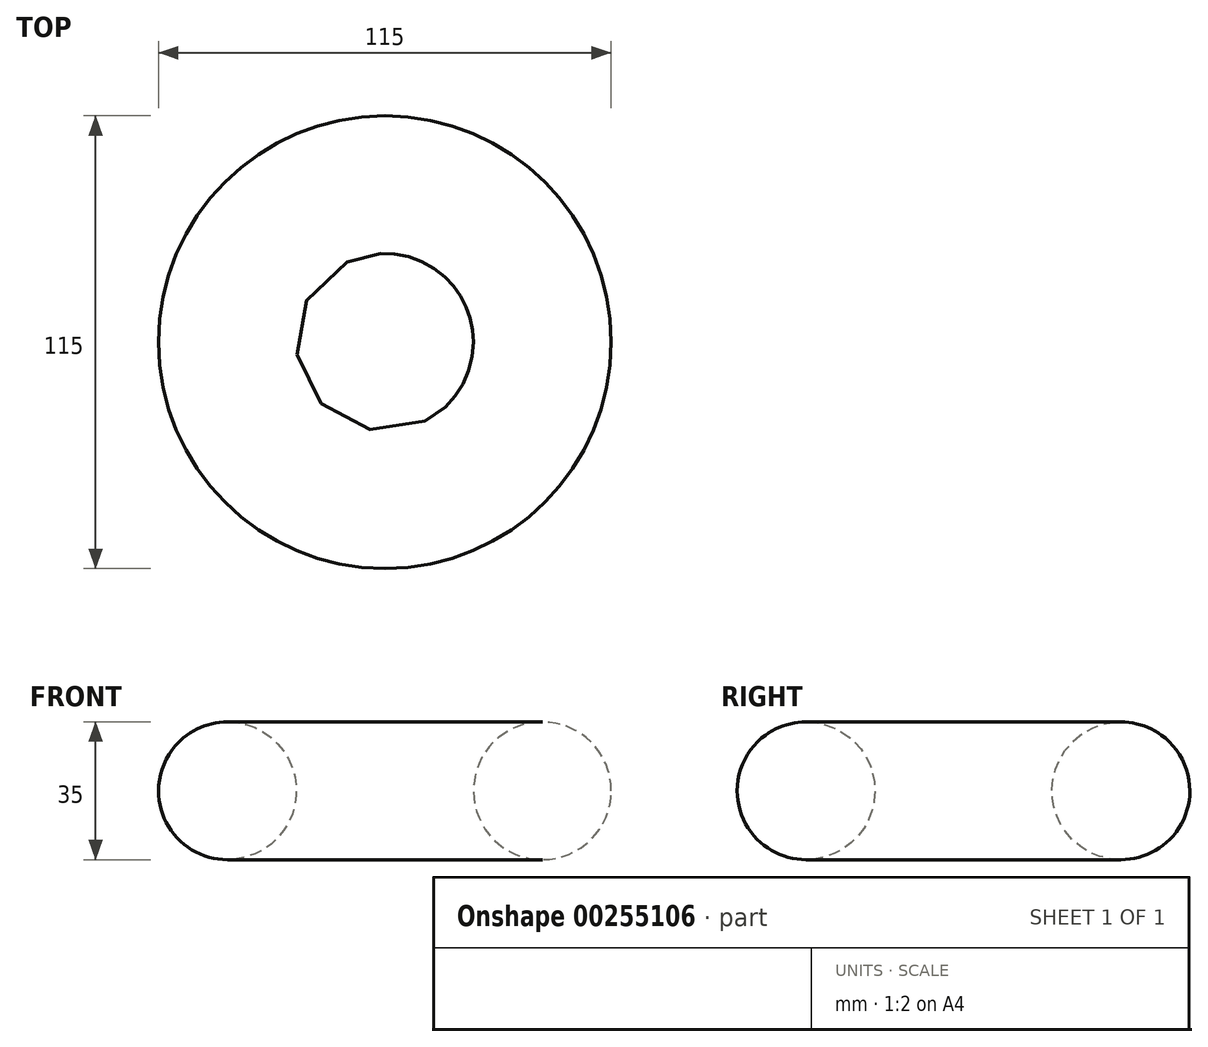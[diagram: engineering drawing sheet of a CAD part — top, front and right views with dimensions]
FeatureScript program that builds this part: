
annotation { "Feature Type Name" : "Feature", "Feature Type Description" : "" }
export const myFeature = defineFeature(function(context is Context, id is Id, definition is map)
    precondition{}
    {
        {
            var Q0;
            Q0=qCreatedBy(makeId("Front.planeOp"),FACE);
            var sketch = newSketch(context, id + "F0", { "sketchPlane" : qUnion([Q0])});
            skCircle(sketch, "E0", {"center": v(40, 0) * mm, "radius": 17.5 * mm});
            skLineSegment(sketch, "E1", {"start": v(0, 39.45) * mm, "end": v(0, -51.78) * mm, "construction": true});
            skSolve(sketch);
        }
        {
            var Q0;
            Q0=makeQuery(id+"F0.imprint","IMPRINT",FACE,{"disambiguationData":[TD([[makeQuery(id+"F0.imprint","IMPRINT",EDGE,{"derivedFrom":sQuery(id+"F0.wireOp",EDGE,"E0")}),1.0]])]});
            var Q1;
            Q1=sQuery(id+"F0.wireOp",EDGE,"E1");
            revolve(context, id + "F1", {"entities" : qUnion([Q0]), "axis" : qUnion([Q1]), "revolveType" : RevolveType.FULL});
        }
    });
